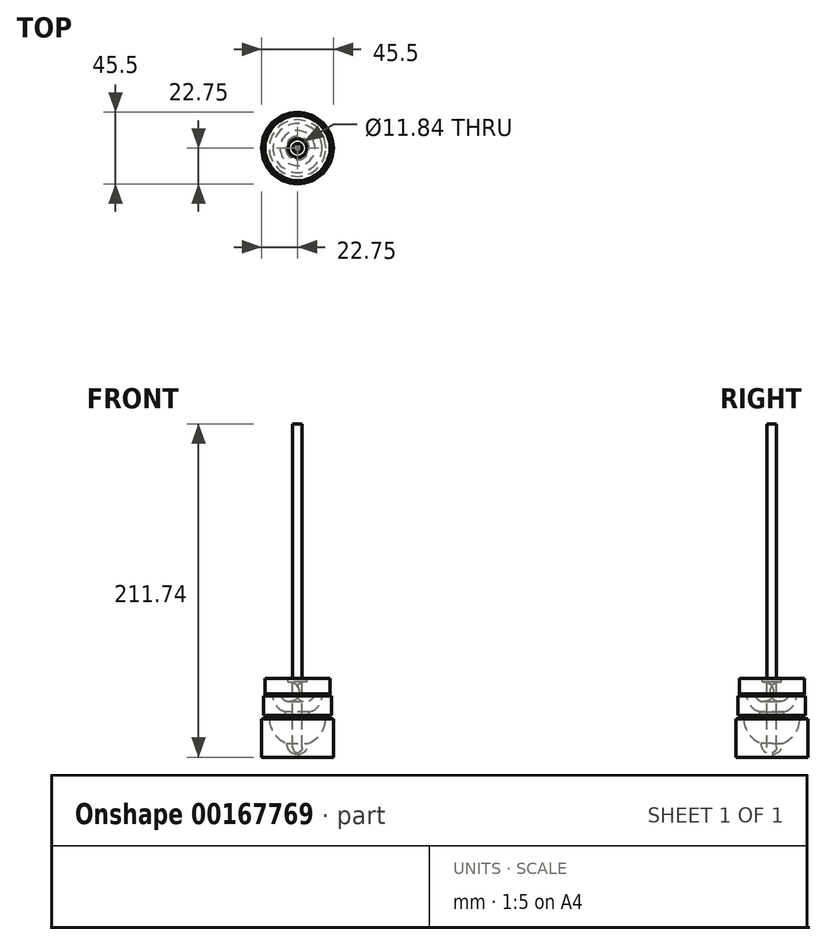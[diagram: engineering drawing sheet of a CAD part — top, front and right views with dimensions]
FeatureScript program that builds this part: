
annotation { "Feature Type Name" : "Feature", "Feature Type Description" : "" }
export const myFeature = defineFeature(function(context is Context, id is Id, definition is map)
    precondition{}
    {
        {
            var Q0;
            Q0=qCreatedBy(makeId("Front.planeOp"),FACE);
            var sketch = newSketch(context, id + "F0", { "sketchPlane" : qUnion([Q0])});
            skArc(sketch, "E0", {"start": v(-7, 0) * mm, "mid": v(-4.95, -4.95) * mm, "end": v(0, -7) * mm});
            skArc(sketch, "E1", {"start": v(-17.97, 15.53) * mm, "mid": v(-14.7, 6.2) * mm, "end": v(-7, 0) * mm});
            skLineSegment(sketch, "E2", {"start": v(-17.97, 15.53) * mm, "end": v(-22.75, 15.53) * mm});
            skLineSegment(sketch, "E3", {"start": v(-22.75, 15.53) * mm, "end": v(-22.75, -8.86) * mm});
            skLineSegment(sketch, "E4", {"start": v(-22.75, -8.86) * mm, "end": v(0, -8.86) * mm});
            skLineSegment(sketch, "E5", {"start": v(0, -8.86) * mm, "end": v(0, -7) * mm});
            skLineSegment(sketch, "E6", {"start": v(0, 21.15) * mm, "end": v(0, -18.22) * mm, "construction": true});
            skSolve(sketch);
        }
        {
            var Q0;
            Q0 = qSketchRegion(id + "F0", true);
            var Q1;
            Q1=sQuery(id+"F0.wireOp",EDGE,"E6");
            revolve(context, id + "F1", {"entities" : qUnion([Q0]), "axis" : qUnion([Q1]), "revolveType" : RevolveType.FULL});
        }
        {
            var Q0;
            Q0=qCreatedBy(makeId("Front.planeOp"),FACE);
            var sketch = newSketch(context, id + "F2", { "sketchPlane" : qUnion([Q0])});
            skArc(sketch, "E7", {"start": v(0, 40) * mm, "mid": v(-10.16, 30) * mm, "end": v(0, 20) * mm});
            skLineSegment(sketch, "E8", {"start": v(0, 51.26) * mm, "end": v(0, 16.43) * mm, "construction": true});
            skSolve(sketch);
        }
        {
            var Q0;
            Q0=sQuery(id+"F2.wireOp",EDGE,"E7");
            var Q1;
            Q1=sQuery(id+"F2.wireOp",EDGE,"E8");
            revolve(context, id + "F3", {"bodyType" : ToolBodyType.SURFACE, "surfaceEntities" : qUnion([Q0]), "axis" : qUnion([Q1]), "revolveType" : RevolveType.FULL});
        }
        {
            var Q0;
            Q0=qCreatedBy(makeId("Front.planeOp"),FACE);
            var sketch = newSketch(context, id + "F4", { "sketchPlane" : qUnion([Q0])});
            skLineSegment(sketch, "E9", {"start": v(-3, 202.88) * mm, "end": v(-3, -2.54) * mm});
            skArc(sketch, "E10", {"start": v(-3, -2.54) * mm, "mid": v(-2.15, -4.84) * mm, "end": v(0, -6.02) * mm});
            skLineSegment(sketch, "E11", {"start": v(0, -8.2) * mm, "end": v(0, 17.84) * mm, "construction": true});
            skPoint(sketch, "E12.orphan", {"position": v(0, 218.2) * mm});
            skLineSegment(sketch, "E13", {"start": v(-3, 202.88) * mm, "end": v(0, 202.88) * mm});
            skLineSegment(sketch, "E14", {"start": v(0, 202.88) * mm, "end": v(0, -6.02) * mm});
            skSolve(sketch);
        }
        {
            var Q0;
            Q0 = qSketchRegion(id + "F4", true);
            var Q1;
            Q1=sQuery(id+"F4.wireOp",EDGE,"E14");
            revolve(context, id + "F5", {"entities" : qUnion([Q0]), "axis" : qUnion([Q1]), "revolveType" : RevolveType.FULL});
        }
        {
            var Q0;
            Q0=qCreatedBy(makeId("Front.planeOp"),FACE);
            var sketch = newSketch(context, id + "F6", { "sketchPlane" : qUnion([Q0])});
            skArc(sketch, "E15", {"start": v(-15.52, 30.15) * mm, "mid": v(-13.27, 23.65) * mm, "end": v(-7.5, 19.9) * mm});
            skLineSegment(sketch, "E16", {"start": v(-21.48, 30.15) * mm, "end": v(-15.52, 30.15) * mm});
            skLineSegment(sketch, "E17", {"start": v(-21.48, 30.15) * mm, "end": v(-21.48, 17.85) * mm});
            skLineSegment(sketch, "E18", {"start": v(-21.48, 17.85) * mm, "end": v(-7.39, 17.85) * mm});
            skLineSegment(sketch, "E19", {"start": v(-7.39, 17.85) * mm, "end": v(-7.5, 19.9) * mm});
            skLineSegment(sketch, "E20", {"start": v(0, 39.46) * mm, "end": v(0, 21.12) * mm, "construction": true});
            skSolve(sketch);
        }
        {
            var Q0;
            Q0 = qSketchRegion(id + "F6", true);
            var Q1;
            Q1=sQuery(id+"F6.wireOp",EDGE,"E20");
            revolve(context, id + "F7", {"entities" : qUnion([Q0]), "axis" : qUnion([Q1]), "revolveType" : RevolveType.FULL});
        }
        {
            var Q0;
            Q0=qCreatedBy(makeId("Front.planeOp"),FACE);
            var sketch = newSketch(context, id + "F8", { "sketchPlane" : qUnion([Q0])});
            skArc(sketch, "E21", {"start": v(-5.92, 38.93) * mm, "mid": v(-10.1, 36.3) * mm, "end": v(-11.08, 31.47) * mm});
            skLineSegment(sketch, "E22", {"start": v(-5.92, 38.93) * mm, "end": v(-5.92, 41.14) * mm});
            skLineSegment(sketch, "E23", {"start": v(-5.92, 41.14) * mm, "end": v(-20.66, 41.14) * mm});
            skLineSegment(sketch, "E24", {"start": v(-20.66, 41.14) * mm, "end": v(-20.66, 31.47) * mm});
            skLineSegment(sketch, "E25", {"start": v(-20.66, 31.47) * mm, "end": v(-11.08, 31.47) * mm});
            skLineSegment(sketch, "E26", {"start": v(0, 45.2) * mm, "end": v(0, 32.76) * mm, "construction": true});
            skSolve(sketch);
        }
        {
            var Q0;
            Q0 = qSketchRegion(id + "F8", true);
            var Q1;
            Q1=sQuery(id+"F8.wireOp",EDGE,"E26");
            revolve(context, id + "F9", {"entities" : qUnion([Q0]), "axis" : qUnion([Q1]), "revolveType" : RevolveType.FULL});
        }
    });
